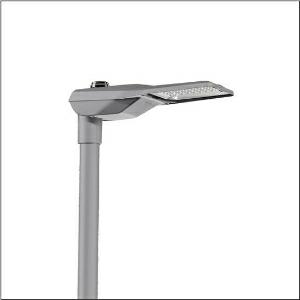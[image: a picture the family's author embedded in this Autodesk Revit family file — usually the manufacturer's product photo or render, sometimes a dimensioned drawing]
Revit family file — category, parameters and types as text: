
# Revit family: streetlight_sl_21_mini___st0_5a_5xe6b37n08gb_187f
name_source: partatom
category: Lighting Fixtures
units: mm (PartAtom-declared; Revit-internal decimal feet)

## family parameters
Cut with Voids When Loaded = No
Host = Face
Light Source = No
Part Type = Normal
Room Calculation Point = No
Round Connector Dimension = Use Diameter
Shared = No

## types (1)
- --- (1 x LED, 5940 lm, 40.4 W, 3000K)
    Apparent Load = 40 VA
    CIE Flux Codes = 41 75 97 100 100
    Color Rendering = 70
    Color Temperature = 3000K
    Default Elevation = 1800 mm
    Description = Streetlight SL 21 mini, mast luminaire, primary light control with lens, of PMMA, primary optical cover: cover, of toughened safety glass, transparent, light distribution: ST0.5a, light emission: direct distribution, primary light characteristic: asymmetric, installation type: side-entry, LED, 3G 1.5mm², High Power LED, rated luminous flux: 5.940lm, luminous efficacy: 147lm/W, light colour: 730, colour temperature: 3000K, control gear: NEMA (7pin), control: overheat protection, pre-setting: linear dimming characteristic, constant luminous flux control, time-dependent luminous flux control, flexible luminous flux parameterisation, mains connection: 230..240V, AC, 50/60Hz, connection cable pre-assembled, cable length: 8,5m, wiring characteristics: H07RN-F, start of lifetime: 40W, end of service life: 41W, reduction: 19W, luminaire housing, of diecast aluminium (EN AC-44300), powder-coated, Siteco® metallic grey (DB 702S), corrosivity category C5 mid according to DIN EN ISO 12944, multi-level sealing system, sealing non-destructively replaceable, inclination adjustable: 0°, 5°, 10°, 15°, length: 628mm, width: 235mm, height: 110mm, spigot size: 42mm (side-entry), mounting height: 4..8m, protection rating (complete): IP66, insulation class (complete): insulation class I (protective earthing), certification: CE, ENEC, ENEC+, VDE, impact resistance: IK10, permissible operating ambient temperature for outdoor applications: -40..+50°C, standard-compliant lighting for roads and squares, packaging unit: 1 piece

Light Distribution: ST0.5a
    Height = 110 mm
    Lamp = 1 x LED
    Lamp Light Flux = 5940 lm
    Lamp Power = 40.4 W
    Lamp count = 1
    Length = 625 mm
    Luminous efficacy = 147 lm/W
    Manufacturer = Siteco
    ModVariant = No
    Model = 5XE6B37N08GB
    Number of Poles = 1
    OnlyDefault = Yes
    Power Factor = 1
    Product Name = Streetlight SL 21 mini | ST0.5a
    Product group = mast luminaire | pylon top
    ProductGroupID = 6100
    Protection Class = Protection class I
    Protection Degree = IP 66
    RLX_Detail_Level = 1
    RLX_Emergency_Light_Flux = 0 lm
    RLX_Emergency_Type = 0
    RLX_Emergency_Type_DB = No
    RlxData = <blob elided: 36813 chars, md5=4fac145b>
    Socket = socket
    Standby Power = 0 W
    System Light Flux = 5940 lm
    System Power = 40 W
    Type Comments = factory setting: luminous flux: 100 % | dim-lin: 254 | 812 mA
    Type Image = l_1294379.jpg
    URL = http://relux.com
    VarID = @adj_159015
    Voltage = 0 V
    Weight = 0.00 kg
    Width = 234 mm

## geometry (parser evidence)
native form markers: Blend x4, Sweep x9
no freeform markers — native parametric forms only
